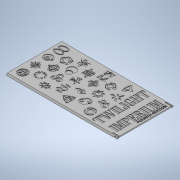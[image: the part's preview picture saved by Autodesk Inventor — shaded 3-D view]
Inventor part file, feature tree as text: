
AUTODESK INVENTOR PART (.ipt)
format: ipt  version: 2021 (Build 250183000, 183)  size: 4,081,152 bytes
history: native  units: mm
features: sketch x4, projected_geometry x4, extrude x3, emboss x1, chamfer x1
ambient origin geometry x8: Origin, YZ Plane, XZ Plane, XY Plane, X Axis, Y Axis, Z Axis, Center Point
bodies: Solid1 (feature_tree)
feature tree (13):
  extrude  "Extrusion1"  Depth=1.5mm
  extrude  "Extrusion2"  Depth=140.85mm TaperAngle=0.0deg
  emboss  "Emboss2"
  extrude  "Extrusion3"  TaperAngle=45.0deg  [1 undecoded]
  chamfer  "Chamfer1"  Distance=0.25mm
  sketch  "Sketch1"  dims[d0=2.0mm d1=1.5mm]
  sketch  "Sketch2"  dims[d2=69.2mm d3=140.85mm d4=0.0mm]
  projected_geometry  "Projected Loop1"
  projected_geometry  "Projected Loop2"
  projected_geometry  "Projected Loop3"
  sketch  "Sketch4"  dims[d5=0.5mm d6=45.0deg]
  projected_geometry  "Projected Loop5"
  sketch  "Sketch5"  dims[d7=0.5mm d8=0.25mm d10=0.6mm d11=60.0deg d12=2.5mm d13=3.0mm d14=0.1mm d15=1.5mm d16=0.8mm d17=8.0mm d18=1.5mm d19=140.85mm d20=0.0mm d25=0.5mm d26=0.0mm d27=25.0mm d28=2.0mm d45=11.487958mm d47=120.0deg d63=0.6mm d64=30.0mm d66=360.0deg d71=45.0deg d76=3.2868mm d78=0.4mm d79=5.5mm d80=40.0mm d82=360.0deg d94=11.280155mm d113=3.4mm d114=5.5mm d116=0.6mm d119=5.977381mm d139=50.0mm d141=360.0deg d147=0.3mm d148=12.566371mm d150=0.3mm d155=2.190066mm d158=0.791849mm d159=0.791849mm d160=6.783034mm d161=5.579043mm d162=1.948844mm d163=1.839132mm d168=5.7mm d169=0.25mm d170=5.4mm d175=0.833136mm d192=0.5mm d199=30.0mm d201=360.0deg d210=120.0deg d211=120.0deg d212=30.0mm d214=360.0deg d219=0.870158mm d226=0.5mm d234=0.5mm d243=0.9mm d246=0.5mm d253=20.0mm d255=360.0deg d258=0.5mm d259=0.5mm d261=0.5mm d263=20.0mm d265=13.962634mm d271=120.0deg d273=4.356856mm d276=1.2mm d279=0.4mm d280=30.0mm d282=360.0deg d291=13.897686mm d292=8.866091mm d305=0.5mm d307=0.5mm d312=20.0mm d314=360.0deg d318=80.0mm d320=360.0deg d329=0.5mm d330=2.0mm d333=9.838812mm d334=2.355924mm d337=0.25mm d338=0.25mm d346=6.253598mm d351=30.0mm d353=360.0deg d360=0.0mm d361=0.0mm d362=60.0mm d364=360.0deg d366=0.5mm d367=2.0mm d368=45.0deg]
note: 1 required parameter value undecoded (feature->parameter linkage not recoverable at this tier; creation-order binding heuristic only, values carry confidence <= 0.55)
